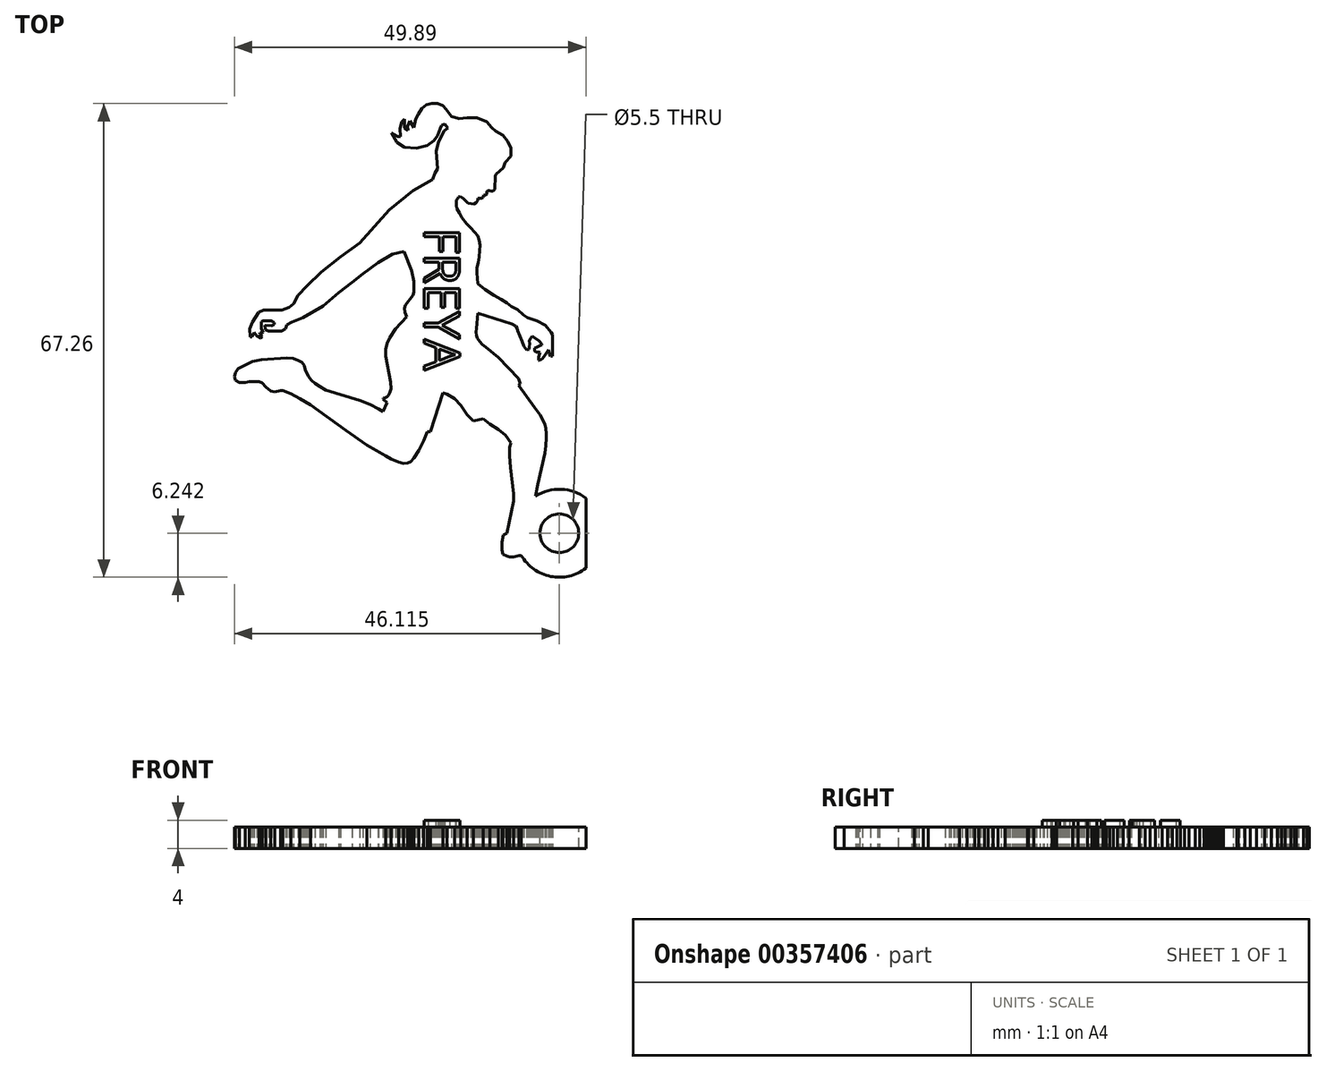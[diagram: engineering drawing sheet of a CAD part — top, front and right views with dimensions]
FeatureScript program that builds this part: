
annotation { "Feature Type Name" : "Feature", "Feature Type Description" : "" }
export const myFeature = defineFeature(function(context is Context, id is Id, definition is map)
    precondition{}
    {
        {
            var Q0;
            Q0=qCreatedBy(makeId("Top.planeOp"),FACE);
            var sketch = newSketch(context, id + "F0", { "sketchPlane" : qUnion([Q0])});
            skLineSegment(sketch, "E0.bottom", {"start": v(0, 0) * mm, "end": v(-50, 0) * mm});
            skLineSegment(sketch, "E0.top", {"start": v(0, 70) * mm, "end": v(-50, 70) * mm});
            skLineSegment(sketch, "E0.left", {"start": v(0, 0) * mm, "end": v(0, 70) * mm});
            skLineSegment(sketch, "E0.right", {"start": v(-50, 0) * mm, "end": v(-50, 70) * mm});
            skLineSegment(sketch, "E1", {"start": v(-9.17, 3.5) * mm, "end": v(-9.48, 3.47) * mm});
            skLineSegment(sketch, "E2", {"start": v(-9.48, 3.47) * mm, "end": v(-10.25, 3.32) * mm});
            skLineSegment(sketch, "E3", {"start": v(-10.25, 3.32) * mm, "end": v(-10.82, 3.32) * mm});
            skLineSegment(sketch, "E4", {"start": v(-10.82, 3.32) * mm, "end": v(-11.24, 3.4) * mm});
            skLineSegment(sketch, "E5", {"start": v(-11.24, 3.4) * mm, "end": v(-11.78, 3.7) * mm});
            skLineSegment(sketch, "E6", {"start": v(-11.78, 3.7) * mm, "end": v(-11.9, 4.28) * mm});
            skLineSegment(sketch, "E7", {"start": v(-11.9, 4.28) * mm, "end": v(-11.9, 5.38) * mm});
            skLineSegment(sketch, "E8", {"start": v(-11.9, 5.38) * mm, "end": v(-11.72, 6.39) * mm});
            skLineSegment(sketch, "E9", {"start": v(-11.72, 6.39) * mm, "end": v(-11.24, 6.64) * mm});
            skLineSegment(sketch, "E10", {"start": v(-11.24, 6.64) * mm, "end": v(-10.25, 11.21) * mm});
            skLineSegment(sketch, "E11", {"start": v(-10.25, 11.21) * mm, "end": v(-10.25, 12.25) * mm});
            skLineSegment(sketch, "E12", {"start": v(-10.25, 12.25) * mm, "end": v(-10.74, 16) * mm});
            skLineSegment(sketch, "E13", {"start": v(-10.74, 16) * mm, "end": v(-10.86, 17.66) * mm});
            skLineSegment(sketch, "E14", {"start": v(-10.86, 17.66) * mm, "end": v(-10.86, 18.84) * mm});
            skLineSegment(sketch, "E15", {"start": v(-10.86, 18.84) * mm, "end": v(-10.66, 19.47) * mm});
            skLineSegment(sketch, "E16", {"start": v(-10.66, 19.47) * mm, "end": v(-11.4, 20.54) * mm});
            skLineSegment(sketch, "E17", {"start": v(-11.4, 20.54) * mm, "end": v(-12.4, 21.37) * mm});
            skLineSegment(sketch, "E18", {"start": v(-12.4, 21.37) * mm, "end": v(-13.64, 22.17) * mm});
            skLineSegment(sketch, "E19", {"start": v(-13.64, 22.17) * mm, "end": v(-14.55, 22.92) * mm});
            skLineSegment(sketch, "E20", {"start": v(-14.55, 22.92) * mm, "end": v(-16, 22.57) * mm});
            skLineSegment(sketch, "E21", {"start": v(-16, 22.57) * mm, "end": v(-16.9, 23.46) * mm});
            skLineSegment(sketch, "E22", {"start": v(-16.9, 23.46) * mm, "end": v(-17.76, 24.82) * mm});
            skLineSegment(sketch, "E23", {"start": v(-17.76, 24.82) * mm, "end": v(-18.67, 25.75) * mm});
            skLineSegment(sketch, "E24", {"start": v(-18.67, 25.75) * mm, "end": v(-19.72, 26.43) * mm});
            skLineSegment(sketch, "E25", {"start": v(-19.72, 26.43) * mm, "end": v(-20.3, 26.61) * mm});
            skLineSegment(sketch, "E26", {"start": v(-20.3, 26.61) * mm, "end": v(-22.05, 21.07) * mm});
            skLineSegment(sketch, "E27", {"start": v(-22.05, 21.07) * mm, "end": v(-22.5, 21.07) * mm});
            skLineSegment(sketch, "E28", {"start": v(-22.5, 21.07) * mm, "end": v(-23.04, 19.78) * mm});
            skLineSegment(sketch, "E29", {"start": v(-23.04, 19.78) * mm, "end": v(-23.74, 18.43) * mm});
            skLineSegment(sketch, "E30", {"start": v(-23.74, 18.43) * mm, "end": v(-24.44, 17.35) * mm});
            skLineSegment(sketch, "E31", {"start": v(-24.44, 17.35) * mm, "end": v(-24.87, 16.83) * mm});
            skLineSegment(sketch, "E32", {"start": v(-24.87, 16.83) * mm, "end": v(-25.32, 16.62) * mm});
            skLineSegment(sketch, "E33", {"start": v(-25.32, 16.62) * mm, "end": v(-25.92, 16.57) * mm});
            skLineSegment(sketch, "E34", {"start": v(-25.92, 16.57) * mm, "end": v(-26.6, 16.74) * mm});
            skLineSegment(sketch, "E35", {"start": v(-26.6, 16.74) * mm, "end": v(-27.67, 17.2) * mm});
            skLineSegment(sketch, "E36", {"start": v(-27.67, 17.2) * mm, "end": v(-28.42, 17.62) * mm});
            skLineSegment(sketch, "E37", {"start": v(-28.42, 17.62) * mm, "end": v(-31.07, 19.17) * mm});
            skLineSegment(sketch, "E38", {"start": v(-31.07, 19.17) * mm, "end": v(-34.05, 21.3) * mm});
            skLineSegment(sketch, "E39", {"start": v(-34.05, 21.3) * mm, "end": v(-39.1, 24.9) * mm});
            skLineSegment(sketch, "E40", {"start": v(-39.1, 24.9) * mm, "end": v(-40.6, 25.77) * mm});
            skLineSegment(sketch, "E41", {"start": v(-40.6, 25.77) * mm, "end": v(-41.87, 26.48) * mm});
            skLineSegment(sketch, "E42", {"start": v(-41.87, 26.48) * mm, "end": v(-43.02, 26.92) * mm});
            skLineSegment(sketch, "E43", {"start": v(-43.02, 26.92) * mm, "end": v(-43.33, 26.92) * mm});
            skLineSegment(sketch, "E44", {"start": v(-43.33, 26.92) * mm, "end": v(-44.18, 26.75) * mm});
            skLineSegment(sketch, "E45", {"start": v(-44.18, 26.75) * mm, "end": v(-44.78, 26.85) * mm});
            skLineSegment(sketch, "E46", {"start": v(-44.78, 26.85) * mm, "end": v(-45.47, 27.43) * mm});
            skLineSegment(sketch, "E47", {"start": v(-45.47, 27.43) * mm, "end": v(-45.94, 27.98) * mm});
            skLineSegment(sketch, "E48", {"start": v(-45.94, 27.98) * mm, "end": v(-46.39, 28.18) * mm});
            skLineSegment(sketch, "E49", {"start": v(-46.39, 28.18) * mm, "end": v(-47.08, 28.18) * mm});
            skLineSegment(sketch, "E50", {"start": v(-47.08, 28.18) * mm, "end": v(-47.78, 28.18) * mm});
            skLineSegment(sketch, "E51", {"start": v(-47.78, 28.18) * mm, "end": v(-48.35, 28.04) * mm});
            skLineSegment(sketch, "E52", {"start": v(-48.35, 28.04) * mm, "end": v(-49.18, 28.04) * mm});
            skLineSegment(sketch, "E53", {"start": v(-49.18, 28.04) * mm, "end": v(-49.76, 28.37) * mm});
            skLineSegment(sketch, "E54", {"start": v(-49.76, 28.37) * mm, "end": v(-49.9, 28.9) * mm});
            skLineSegment(sketch, "E55", {"start": v(-49.9, 28.9) * mm, "end": v(-49.8, 29.43) * mm});
            skLineSegment(sketch, "E56", {"start": v(-49.8, 29.43) * mm, "end": v(-49.4, 30.04) * mm});
            skLineSegment(sketch, "E57", {"start": v(-49.4, 30.04) * mm, "end": v(-48.36, 30.54) * mm});
            skLineSegment(sketch, "E58", {"start": v(-48.36, 30.54) * mm, "end": v(-47.36, 31.02) * mm});
            skLineSegment(sketch, "E59", {"start": v(-47.36, 31.02) * mm, "end": v(-46.1, 31.27) * mm});
            skLineSegment(sketch, "E60", {"start": v(-46.1, 31.27) * mm, "end": v(-44.89, 31.37) * mm});
            skLineSegment(sketch, "E61", {"start": v(-44.89, 31.37) * mm, "end": v(-43.62, 31.47) * mm});
            skLineSegment(sketch, "E62", {"start": v(-43.62, 31.47) * mm, "end": v(-42.48, 31.56) * mm});
            skLineSegment(sketch, "E63", {"start": v(-42.48, 31.56) * mm, "end": v(-41.57, 31.5) * mm});
            skLineSegment(sketch, "E64", {"start": v(-41.57, 31.5) * mm, "end": v(-40.79, 31.19) * mm});
            skLineSegment(sketch, "E65", {"start": v(-40.79, 31.19) * mm, "end": v(-40.32, 30.92) * mm});
            skLineSegment(sketch, "E66", {"start": v(-40.32, 30.92) * mm, "end": v(-40, 30.5) * mm});
            skLineSegment(sketch, "E67", {"start": v(-40, 30.5) * mm, "end": v(-39.86, 29.9) * mm});
            skLineSegment(sketch, "E68", {"start": v(-39.86, 29.9) * mm, "end": v(-39.65, 29.47) * mm});
            skLineSegment(sketch, "E69", {"start": v(-39.65, 29.47) * mm, "end": v(-39.4, 28.93) * mm});
            skLineSegment(sketch, "E70", {"start": v(-39.4, 28.93) * mm, "end": v(-38.97, 28.35) * mm});
            skLineSegment(sketch, "E71", {"start": v(-38.97, 28.35) * mm, "end": v(-38.46, 27.9) * mm});
            skLineSegment(sketch, "E72", {"start": v(-38.46, 27.9) * mm, "end": v(-37.78, 27.46) * mm});
            skLineSegment(sketch, "E73", {"start": v(-37.78, 27.46) * mm, "end": v(-36.91, 27) * mm});
            skLineSegment(sketch, "E74", {"start": v(-36.91, 27) * mm, "end": v(-35.94, 26.7) * mm});
            skLineSegment(sketch, "E75", {"start": v(-35.94, 26.7) * mm, "end": v(-34.76, 26.33) * mm});
            skLineSegment(sketch, "E76", {"start": v(-34.76, 26.33) * mm, "end": v(-32.12, 25.5) * mm});
            skLineSegment(sketch, "E77", {"start": v(-32.12, 25.5) * mm, "end": v(-30.66, 24.93) * mm});
            skLineSegment(sketch, "E78", {"start": v(-30.66, 24.93) * mm, "end": v(-29.45, 24.33) * mm});
            skLineSegment(sketch, "E79", {"start": v(-29.45, 24.33) * mm, "end": v(-28.83, 23.93) * mm});
            skLineSegment(sketch, "E80", {"start": v(-28.83, 23.93) * mm, "end": v(-28.21, 25.2) * mm});
            skLineSegment(sketch, "E81", {"start": v(-28.21, 25.2) * mm, "end": v(-28.82, 25.7) * mm});
            skLineSegment(sketch, "E82", {"start": v(-28.82, 25.7) * mm, "end": v(-28.76, 25.81) * mm});
            skLineSegment(sketch, "E83", {"start": v(-28.76, 25.81) * mm, "end": v(-28.5, 25.88) * mm});
            skLineSegment(sketch, "E84", {"start": v(-28.5, 25.88) * mm, "end": v(-28.24, 26) * mm});
            skLineSegment(sketch, "E85", {"start": v(-28.24, 26) * mm, "end": v(-28.06, 26.23) * mm});
            skLineSegment(sketch, "E86", {"start": v(-28.06, 26.23) * mm, "end": v(-27.83, 26.57) * mm});
            skLineSegment(sketch, "E87", {"start": v(-27.83, 26.57) * mm, "end": v(-27.65, 27.16) * mm});
            skLineSegment(sketch, "E88", {"start": v(-27.65, 27.16) * mm, "end": v(-27.72, 28.1) * mm});
            skLineSegment(sketch, "E89", {"start": v(-27.72, 28.1) * mm, "end": v(-27.93, 29.16) * mm});
            skLineSegment(sketch, "E90", {"start": v(-27.93, 29.16) * mm, "end": v(-28.21, 30.56) * mm});
            skLineSegment(sketch, "E91", {"start": v(-28.21, 30.56) * mm, "end": v(-28.46, 31.8) * mm});
            skLineSegment(sketch, "E92", {"start": v(-28.46, 31.8) * mm, "end": v(-28.4, 32.79) * mm});
            skLineSegment(sketch, "E93", {"start": v(-28.4, 32.79) * mm, "end": v(-28.21, 33.59) * mm});
            skLineSegment(sketch, "E94", {"start": v(-28.21, 33.59) * mm, "end": v(-27.88, 34.42) * mm});
            skLineSegment(sketch, "E95", {"start": v(-27.88, 34.42) * mm, "end": v(-27.04, 35.7) * mm});
            skLineSegment(sketch, "E96", {"start": v(-27.04, 35.7) * mm, "end": v(-25.43, 37.42) * mm});
            skLineSegment(sketch, "E97", {"start": v(-25.43, 37.42) * mm, "end": v(-25.71, 38) * mm});
            skLineSegment(sketch, "E98", {"start": v(-25.71, 38) * mm, "end": v(-25.76, 38.6) * mm});
            skLineSegment(sketch, "E99", {"start": v(-25.76, 38.6) * mm, "end": v(-25.65, 39.06) * mm});
            skLineSegment(sketch, "E100", {"start": v(-25.65, 39.06) * mm, "end": v(-25.11, 39.71) * mm});
            skLineSegment(sketch, "E101", {"start": v(-25.11, 39.71) * mm, "end": v(-24.53, 40.43) * mm});
            skLineSegment(sketch, "E102", {"start": v(-24.53, 40.43) * mm, "end": v(-24.44, 40.9) * mm});
            skLineSegment(sketch, "E103", {"start": v(-24.44, 40.9) * mm, "end": v(-24.44, 42.39) * mm});
            skLineSegment(sketch, "E104", {"start": v(-24.44, 42.39) * mm, "end": v(-24.74, 43.9) * mm});
            skLineSegment(sketch, "E105", {"start": v(-24.74, 43.9) * mm, "end": v(-25.83, 46.69) * mm});
            skLineSegment(sketch, "E106", {"start": v(-25.83, 46.69) * mm, "end": v(-27.46, 46.29) * mm});
            skLineSegment(sketch, "E107", {"start": v(-27.46, 46.29) * mm, "end": v(-29.5, 45.05) * mm});
            skLineSegment(sketch, "E108", {"start": v(-29.5, 45.05) * mm, "end": v(-31.65, 43.48) * mm});
            skLineSegment(sketch, "E109", {"start": v(-31.65, 43.48) * mm, "end": v(-33.2, 42.3) * mm});
            skLineSegment(sketch, "E110", {"start": v(-33.2, 42.3) * mm, "end": v(-35.08, 40.8) * mm});
            skLineSegment(sketch, "E111", {"start": v(-35.08, 40.8) * mm, "end": v(-37.3, 38.93) * mm});
            skLineSegment(sketch, "E112", {"start": v(-37.3, 38.93) * mm, "end": v(-40.15, 37.27) * mm});
            skLineSegment(sketch, "E113", {"start": v(-40.15, 37.27) * mm, "end": v(-41.8, 36.64) * mm});
            skLineSegment(sketch, "E114", {"start": v(-41.8, 36.64) * mm, "end": v(-42.44, 36.27) * mm});
            skLineSegment(sketch, "E115", {"start": v(-42.44, 36.27) * mm, "end": v(-42.67, 35.69) * mm});
            skLineSegment(sketch, "E116", {"start": v(-42.67, 35.69) * mm, "end": v(-43.2, 35.37) * mm});
            skLineSegment(sketch, "E117", {"start": v(-43.2, 35.37) * mm, "end": v(-45.06, 35.37) * mm});
            skLineSegment(sketch, "E118", {"start": v(-45.06, 35.37) * mm, "end": v(-45.52, 35.56) * mm});
            skLineSegment(sketch, "E119", {"start": v(-45.52, 35.56) * mm, "end": v(-45.57, 36.16) * mm});
            skLineSegment(sketch, "E120", {"start": v(-45.57, 36.16) * mm, "end": v(-44.6, 36.1) * mm});
            skLineSegment(sketch, "E121", {"start": v(-44.6, 36.1) * mm, "end": v(-44.22, 36.28) * mm});
            skLineSegment(sketch, "E122", {"start": v(-44.22, 36.28) * mm, "end": v(-44.22, 36.58) * mm});
            skLineSegment(sketch, "E123", {"start": v(-44.22, 36.58) * mm, "end": v(-44.69, 36.85) * mm});
            skLineSegment(sketch, "E124", {"start": v(-44.69, 36.85) * mm, "end": v(-45.84, 36.8) * mm});
            skLineSegment(sketch, "E125", {"start": v(-45.84, 36.8) * mm, "end": v(-46.08, 36.67) * mm});
            skLineSegment(sketch, "E126", {"start": v(-46.08, 36.67) * mm, "end": v(-46.08, 35.72) * mm});
            skLineSegment(sketch, "E127", {"start": v(-46.08, 35.72) * mm, "end": v(-45.82, 35.2) * mm});
            skLineSegment(sketch, "E128", {"start": v(-45.82, 35.2) * mm, "end": v(-45.87, 35.08) * mm});
            skLineSegment(sketch, "E129", {"start": v(-45.87, 35.08) * mm, "end": v(-46.27, 35.08) * mm});
            skLineSegment(sketch, "E130", {"start": v(-46.27, 35.08) * mm, "end": v(-46.3, 34.93) * mm});
            skLineSegment(sketch, "E131", {"start": v(-46.3, 34.93) * mm, "end": v(-45.94, 34.61) * mm});
            skLineSegment(sketch, "E132", {"start": v(-45.94, 34.61) * mm, "end": v(-46.16, 34.34) * mm});
            skLineSegment(sketch, "E133", {"start": v(-46.16, 34.34) * mm, "end": v(-46.7, 34.65) * mm});
            skLineSegment(sketch, "E134", {"start": v(-46.7, 34.65) * mm, "end": v(-47.11, 35.15) * mm});
            skLineSegment(sketch, "E135", {"start": v(-47.11, 35.15) * mm, "end": v(-47.42, 34.54) * mm});
            skLineSegment(sketch, "E136", {"start": v(-47.42, 34.54) * mm, "end": v(-47.66, 34.54) * mm});
            skLineSegment(sketch, "E137", {"start": v(-47.66, 34.54) * mm, "end": v(-47.76, 35.69) * mm});
            skLineSegment(sketch, "E138", {"start": v(-47.76, 35.69) * mm, "end": v(-47.37, 36.65) * mm});
            skLineSegment(sketch, "E139", {"start": v(-47.37, 36.65) * mm, "end": v(-46.5, 38) * mm});
            skLineSegment(sketch, "E140", {"start": v(-46.5, 38) * mm, "end": v(-45.76, 38.35) * mm});
            skLineSegment(sketch, "E141", {"start": v(-45.76, 38.35) * mm, "end": v(-43.14, 38.35) * mm});
            skLineSegment(sketch, "E142", {"start": v(-43.14, 38.35) * mm, "end": v(-42.18, 38.72) * mm});
            skLineSegment(sketch, "E143", {"start": v(-42.18, 38.72) * mm, "end": v(-41.51, 39.25) * mm});
            skLineSegment(sketch, "E144", {"start": v(-41.51, 39.25) * mm, "end": v(-40.85, 40.43) * mm});
            skLineSegment(sketch, "E145", {"start": v(-40.85, 40.43) * mm, "end": v(-39.6, 41.78) * mm});
            skLineSegment(sketch, "E146", {"start": v(-39.6, 41.78) * mm, "end": v(-37.56, 43.72) * mm});
            skLineSegment(sketch, "E147", {"start": v(-37.56, 43.72) * mm, "end": v(-34.86, 45.88) * mm});
            skLineSegment(sketch, "E148", {"start": v(-34.86, 45.88) * mm, "end": v(-32.12, 47.88) * mm});
            skLineSegment(sketch, "E149", {"start": v(-32.12, 47.88) * mm, "end": v(-27.93, 52.55) * mm});
            skLineSegment(sketch, "E150", {"start": v(-27.93, 52.55) * mm, "end": v(-24.53, 55.27) * mm});
            skLineSegment(sketch, "E151", {"start": v(-24.53, 55.27) * mm, "end": v(-21.79, 56.87) * mm});
            skLineSegment(sketch, "E152", {"start": v(-21.79, 56.87) * mm, "end": v(-21.43, 57.77) * mm});
            skLineSegment(sketch, "E153", {"start": v(-21.43, 57.77) * mm, "end": v(-21.03, 58.38) * mm});
            skLineSegment(sketch, "E154", {"start": v(-21.03, 58.38) * mm, "end": v(-21.23, 60.88) * mm});
            skLineSegment(sketch, "E155", {"start": v(-21.23, 60.88) * mm, "end": v(-20.92, 62.2) * mm});
            skLineSegment(sketch, "E156", {"start": v(-20.92, 62.2) * mm, "end": v(-20.5, 63.07) * mm});
            skLineSegment(sketch, "E157", {"start": v(-20.5, 63.07) * mm, "end": v(-20.13, 63.82) * mm});
            skLineSegment(sketch, "E158", {"start": v(-20.13, 63.82) * mm, "end": v(-19.63, 64.22) * mm});
            skLineSegment(sketch, "E159", {"start": v(-19.63, 64.22) * mm, "end": v(-20.06, 64.75) * mm});
            skLineSegment(sketch, "E160", {"start": v(-20.06, 64.75) * mm, "end": v(-20.5, 64.54) * mm});
            skLineSegment(sketch, "E161", {"start": v(-20.5, 64.54) * mm, "end": v(-20.7, 64.13) * mm});
            skLineSegment(sketch, "E162", {"start": v(-20.7, 64.13) * mm, "end": v(-21.03, 63.08) * mm});
            skLineSegment(sketch, "E163", {"start": v(-21.03, 63.08) * mm, "end": v(-21.56, 62.44) * mm});
            skLineSegment(sketch, "E164", {"start": v(-21.56, 62.44) * mm, "end": v(-22.5, 61.68) * mm});
            skLineSegment(sketch, "E165", {"start": v(-22.5, 61.68) * mm, "end": v(-24.04, 61.3) * mm});
            skLineSegment(sketch, "E166", {"start": v(-24.04, 61.3) * mm, "end": v(-25.76, 61.46) * mm});
            skLineSegment(sketch, "E167", {"start": v(-25.76, 61.46) * mm, "end": v(-26.81, 62.15) * mm});
            skLineSegment(sketch, "E168", {"start": v(-26.81, 62.15) * mm, "end": v(-27.6, 63.51) * mm});
            skLineSegment(sketch, "E169", {"start": v(-27.6, 63.51) * mm, "end": v(-26.72, 63) * mm});
            skLineSegment(sketch, "E170", {"start": v(-26.72, 63) * mm, "end": v(-26.35, 63) * mm});
            skLineSegment(sketch, "E171", {"start": v(-26.35, 63) * mm, "end": v(-26.4, 64.13) * mm});
            skLineSegment(sketch, "E172", {"start": v(-26.4, 64.13) * mm, "end": v(-26.14, 65.05) * mm});
            skLineSegment(sketch, "E173", {"start": v(-26.14, 65.05) * mm, "end": v(-25.76, 65.44) * mm});
            skLineSegment(sketch, "E174", {"start": v(-25.76, 65.44) * mm, "end": v(-25.76, 64.64) * mm});
            skLineSegment(sketch, "E175", {"start": v(-25.76, 64.64) * mm, "end": v(-25.76, 64.19) * mm});
            skLineSegment(sketch, "E176", {"start": v(-25.76, 64.19) * mm, "end": v(-25.29, 63.88) * mm});
            skLineSegment(sketch, "E177", {"start": v(-25.29, 63.88) * mm, "end": v(-25.33, 64.43) * mm});
            skLineSegment(sketch, "E178", {"start": v(-25.33, 64.43) * mm, "end": v(-25, 65.17) * mm});
            skLineSegment(sketch, "E179", {"start": v(-25, 65.17) * mm, "end": v(-24.44, 64.22) * mm});
            skLineSegment(sketch, "E180", {"start": v(-24.44, 64.22) * mm, "end": v(-24.16, 65.43) * mm});
            skLineSegment(sketch, "E181", {"start": v(-24.16, 65.43) * mm, "end": v(-23.8, 66.17) * mm});
            skLineSegment(sketch, "E182", {"start": v(-23.8, 66.17) * mm, "end": v(-23.26, 67) * mm});
            skLineSegment(sketch, "E183", {"start": v(-23.26, 67) * mm, "end": v(-22.65, 67.48) * mm});
            skLineSegment(sketch, "E184", {"start": v(-22.65, 67.48) * mm, "end": v(-21.89, 67.67) * mm});
            skLineSegment(sketch, "E185", {"start": v(-21.89, 67.67) * mm, "end": v(-21.04, 67.66) * mm});
            skLineSegment(sketch, "E186", {"start": v(-21.04, 67.66) * mm, "end": v(-20.3, 67.4) * mm});
            skLineSegment(sketch, "E187", {"start": v(-20.3, 67.4) * mm, "end": v(-19.86, 66.83) * mm});
            skLineSegment(sketch, "E188", {"start": v(-19.86, 66.83) * mm, "end": v(-19.09, 65.86) * mm});
            skLineSegment(sketch, "E189", {"start": v(-19.09, 65.86) * mm, "end": v(-18.02, 65.52) * mm});
            skLineSegment(sketch, "E190", {"start": v(-18.02, 65.52) * mm, "end": v(-16.84, 65.62) * mm});
            skLineSegment(sketch, "E191", {"start": v(-16.84, 65.62) * mm, "end": v(-15.47, 65.62) * mm});
            skLineSegment(sketch, "E192", {"start": v(-15.47, 65.62) * mm, "end": v(-14.09, 65.06) * mm});
            skLineSegment(sketch, "E193", {"start": v(-14.09, 65.06) * mm, "end": v(-13.36, 64.27) * mm});
            skLineSegment(sketch, "E194", {"start": v(-13.36, 64.27) * mm, "end": v(-12.84, 63.75) * mm});
            skLineSegment(sketch, "E195", {"start": v(-12.84, 63.75) * mm, "end": v(-11.78, 63.15) * mm});
            skLineSegment(sketch, "E196", {"start": v(-11.78, 63.15) * mm, "end": v(-11.1, 62.3) * mm});
            skLineSegment(sketch, "E197", {"start": v(-11.1, 62.3) * mm, "end": v(-10.62, 61.3) * mm});
            skLineSegment(sketch, "E198", {"start": v(-10.62, 61.3) * mm, "end": v(-10.62, 60.2) * mm});
            skLineSegment(sketch, "E199", {"start": v(-10.62, 60.2) * mm, "end": v(-11.5, 59.28) * mm});
            skLineSegment(sketch, "E200", {"start": v(-11.5, 59.28) * mm, "end": v(-11.73, 58.55) * mm});
            skLineSegment(sketch, "E201", {"start": v(-11.73, 58.55) * mm, "end": v(-12.75, 57.62) * mm});
            skLineSegment(sketch, "E202", {"start": v(-12.75, 57.62) * mm, "end": v(-12.87, 57.37) * mm});
            skLineSegment(sketch, "E203", {"start": v(-12.87, 57.37) * mm, "end": v(-12.95, 55.5) * mm});
            skLineSegment(sketch, "E204", {"start": v(-12.95, 55.5) * mm, "end": v(-13.03, 55.35) * mm});
            skLineSegment(sketch, "E205", {"start": v(-13.03, 55.35) * mm, "end": v(-13.19, 55.22) * mm});
            skLineSegment(sketch, "E206", {"start": v(-13.19, 55.22) * mm, "end": v(-13.42, 55.22) * mm});
            skLineSegment(sketch, "E207", {"start": v(-13.42, 55.22) * mm, "end": v(-13.68, 55.27) * mm});
            skLineSegment(sketch, "E208", {"start": v(-13.68, 55.27) * mm, "end": v(-13.95, 55.27) * mm});
            skLineSegment(sketch, "E209", {"start": v(-13.95, 55.27) * mm, "end": v(-14.04, 55.22) * mm});
            skLineSegment(sketch, "E210", {"start": v(-14.04, 55.22) * mm, "end": v(-14.08, 55.02) * mm});
            skLineSegment(sketch, "E211", {"start": v(-14.08, 55.02) * mm, "end": v(-14.08, 54.8) * mm});
            skLineSegment(sketch, "E212", {"start": v(-14.08, 54.8) * mm, "end": v(-14.2, 54.7) * mm});
            skLineSegment(sketch, "E213", {"start": v(-14.2, 54.7) * mm, "end": v(-14.53, 54.67) * mm});
            skLineSegment(sketch, "E214", {"start": v(-14.53, 54.67) * mm, "end": v(-14.59, 54.36) * mm});
            skLineSegment(sketch, "E215", {"start": v(-14.59, 54.36) * mm, "end": v(-14.7, 54.25) * mm});
            skLineSegment(sketch, "E216", {"start": v(-14.7, 54.25) * mm, "end": v(-14.85, 54.2) * mm});
            skLineSegment(sketch, "E217", {"start": v(-14.85, 54.2) * mm, "end": v(-15.37, 54.2) * mm});
            skLineSegment(sketch, "E218", {"start": v(-15.37, 54.2) * mm, "end": v(-15.34, 53.88) * mm});
            skLineSegment(sketch, "E219", {"start": v(-15.34, 53.88) * mm, "end": v(-15.58, 53.57) * mm});
            skLineSegment(sketch, "E220", {"start": v(-15.58, 53.57) * mm, "end": v(-15.92, 53.4) * mm});
            skLineSegment(sketch, "E221", {"start": v(-15.92, 53.4) * mm, "end": v(-16.32, 53.45) * mm});
            skLineSegment(sketch, "E222", {"start": v(-16.32, 53.45) * mm, "end": v(-16.73, 53.53) * mm});
            skLineSegment(sketch, "E223", {"start": v(-16.73, 53.53) * mm, "end": v(-17.08, 53.82) * mm});
            skLineSegment(sketch, "E224", {"start": v(-17.08, 53.82) * mm, "end": v(-17.4, 54.12) * mm});
            skLineSegment(sketch, "E225", {"start": v(-17.4, 54.12) * mm, "end": v(-17.62, 54.37) * mm});
            skLineSegment(sketch, "E226", {"start": v(-17.62, 54.37) * mm, "end": v(-17.83, 54.47) * mm});
            skLineSegment(sketch, "E227", {"start": v(-17.83, 54.47) * mm, "end": v(-18.06, 54.41) * mm});
            skLineSegment(sketch, "E228", {"start": v(-18.06, 54.41) * mm, "end": v(-18.21, 54.15) * mm});
            skLineSegment(sketch, "E229", {"start": v(-18.21, 54.15) * mm, "end": v(-18.38, 53.94) * mm});
            skLineSegment(sketch, "E230", {"start": v(-18.38, 53.94) * mm, "end": v(-18.43, 53.67) * mm});
            skLineSegment(sketch, "E231", {"start": v(-18.43, 53.67) * mm, "end": v(-18.39, 53.2) * mm});
            skLineSegment(sketch, "E232", {"start": v(-18.39, 53.2) * mm, "end": v(-18.3, 52.76) * mm});
            skLineSegment(sketch, "E233", {"start": v(-18.3, 52.76) * mm, "end": v(-17.93, 52.1) * mm});
            skLineSegment(sketch, "E234", {"start": v(-17.93, 52.1) * mm, "end": v(-17.62, 51.46) * mm});
            skLineSegment(sketch, "E235", {"start": v(-17.62, 51.46) * mm, "end": v(-16.95, 50.63) * mm});
            skLineSegment(sketch, "E236", {"start": v(-16.95, 50.63) * mm, "end": v(-16.35, 50) * mm});
            skLineSegment(sketch, "E237", {"start": v(-16.35, 50) * mm, "end": v(-15.77, 49.42) * mm});
            skLineSegment(sketch, "E238", {"start": v(-15.77, 49.42) * mm, "end": v(-15.38, 48.9) * mm});
            skLineSegment(sketch, "E239", {"start": v(-15.38, 48.9) * mm, "end": v(-15.14, 48.22) * mm});
            skLineSegment(sketch, "E240", {"start": v(-15.14, 48.22) * mm, "end": v(-15.04, 47.53) * mm});
            skLineSegment(sketch, "E241", {"start": v(-15.04, 47.53) * mm, "end": v(-15.07, 46.8) * mm});
            skLineSegment(sketch, "E242", {"start": v(-15.07, 46.8) * mm, "end": v(-15.13, 45.87) * mm});
            skLineSegment(sketch, "E243", {"start": v(-15.13, 45.87) * mm, "end": v(-15.27, 45.06) * mm});
            skLineSegment(sketch, "E244", {"start": v(-15.27, 45.06) * mm, "end": v(-15.48, 44.4) * mm});
            skLineSegment(sketch, "E245", {"start": v(-15.48, 44.4) * mm, "end": v(-15.45, 43.59) * mm});
            skLineSegment(sketch, "E246", {"start": v(-15.45, 43.59) * mm, "end": v(-15.38, 42.71) * mm});
            skLineSegment(sketch, "E247", {"start": v(-15.38, 42.71) * mm, "end": v(-15.34, 42.1) * mm});
            skLineSegment(sketch, "E248", {"start": v(-15.34, 42.1) * mm, "end": v(-14.31, 41.26) * mm});
            skLineSegment(sketch, "E249", {"start": v(-14.31, 41.26) * mm, "end": v(-13.09, 40.43) * mm});
            skLineSegment(sketch, "E250", {"start": v(-13.09, 40.43) * mm, "end": v(-12.07, 39.87) * mm});
            skLineSegment(sketch, "E251", {"start": v(-12.07, 39.87) * mm, "end": v(-11.24, 39.35) * mm});
            skLineSegment(sketch, "E252", {"start": v(-11.24, 39.35) * mm, "end": v(-10.57, 38.84) * mm});
            skLineSegment(sketch, "E253", {"start": v(-10.57, 38.84) * mm, "end": v(-9.71, 38.39) * mm});
            skLineSegment(sketch, "E254", {"start": v(-9.71, 38.39) * mm, "end": v(-8.87, 37.67) * mm});
            skLineSegment(sketch, "E255", {"start": v(-8.87, 37.67) * mm, "end": v(-8.32, 37.28) * mm});
            skLineSegment(sketch, "E256", {"start": v(-8.32, 37.28) * mm, "end": v(-6.94, 36.85) * mm});
            skLineSegment(sketch, "E257", {"start": v(-6.94, 36.85) * mm, "end": v(-5.79, 36.17) * mm});
            skLineSegment(sketch, "E258", {"start": v(-5.79, 36.17) * mm, "end": v(-4.96, 35.15) * mm});
            skLineSegment(sketch, "E259", {"start": v(-4.96, 35.15) * mm, "end": v(-4.72, 34.85) * mm});
            skLineSegment(sketch, "E260", {"start": v(-4.72, 34.85) * mm, "end": v(-4.75, 34.08) * mm});
            skLineSegment(sketch, "E261", {"start": v(-4.75, 34.08) * mm, "end": v(-4.75, 33.59) * mm});
            skLineSegment(sketch, "E262", {"start": v(-4.75, 33.59) * mm, "end": v(-4.75, 31.8) * mm});
            skLineSegment(sketch, "E263", {"start": v(-4.75, 31.8) * mm, "end": v(-4.98, 31.8) * mm});
            skLineSegment(sketch, "E264", {"start": v(-4.98, 31.8) * mm, "end": v(-5.22, 32.11) * mm});
            skLineSegment(sketch, "E265", {"start": v(-5.22, 32.11) * mm, "end": v(-5.33, 32.68) * mm});
            skLineSegment(sketch, "E266", {"start": v(-5.33, 32.68) * mm, "end": v(-5.8, 31.94) * mm});
            skLineSegment(sketch, "E267", {"start": v(-5.8, 31.94) * mm, "end": v(-6.17, 31.48) * mm});
            skLineSegment(sketch, "E268", {"start": v(-6.17, 31.48) * mm, "end": v(-6.57, 31.16) * mm});
            skLineSegment(sketch, "E269", {"start": v(-6.57, 31.16) * mm, "end": v(-6.7, 31.2) * mm});
            skLineSegment(sketch, "E270", {"start": v(-6.7, 31.2) * mm, "end": v(-6.7, 31.68) * mm});
            skLineSegment(sketch, "E271", {"start": v(-6.7, 31.68) * mm, "end": v(-6.6, 32.1) * mm});
            skLineSegment(sketch, "E272", {"start": v(-6.6, 32.1) * mm, "end": v(-6.51, 32.28) * mm});
            skLineSegment(sketch, "E273", {"start": v(-6.51, 32.28) * mm, "end": v(-6.62, 32.38) * mm});
            skLineSegment(sketch, "E274", {"start": v(-6.62, 32.38) * mm, "end": v(-7.06, 32.38) * mm});
            skLineSegment(sketch, "E275", {"start": v(-7.06, 32.38) * mm, "end": v(-7.27, 32.47) * mm});
            skLineSegment(sketch, "E276", {"start": v(-7.27, 32.47) * mm, "end": v(-7.3, 32.68) * mm});
            skLineSegment(sketch, "E277", {"start": v(-7.3, 32.68) * mm, "end": v(-7.3, 32.95) * mm});
            skLineSegment(sketch, "E278", {"start": v(-7.3, 32.95) * mm, "end": v(-6.99, 33.1) * mm});
            skLineSegment(sketch, "E279", {"start": v(-6.99, 33.1) * mm, "end": v(-6.61, 33.28) * mm});
            skLineSegment(sketch, "E280", {"start": v(-6.61, 33.28) * mm, "end": v(-6.27, 33.36) * mm});
            skLineSegment(sketch, "E281", {"start": v(-6.27, 33.36) * mm, "end": v(-6.25, 33.53) * mm});
            skLineSegment(sketch, "E282", {"start": v(-6.25, 33.53) * mm, "end": v(-6.66, 33.96) * mm});
            skLineSegment(sketch, "E283", {"start": v(-6.66, 33.96) * mm, "end": v(-7.46, 34.54) * mm});
            skLineSegment(sketch, "E284", {"start": v(-7.46, 34.54) * mm, "end": v(-7.69, 34.61) * mm});
            skLineSegment(sketch, "E285", {"start": v(-7.69, 34.61) * mm, "end": v(-7.84, 34.34) * mm});
            skLineSegment(sketch, "E286", {"start": v(-7.84, 34.34) * mm, "end": v(-8.05, 33.99) * mm});
            skLineSegment(sketch, "E287", {"start": v(-8.05, 33.99) * mm, "end": v(-8, 33.59) * mm});
            skLineSegment(sketch, "E288", {"start": v(-8, 33.59) * mm, "end": v(-8.07, 33.04) * mm});
            skLineSegment(sketch, "E289", {"start": v(-8.07, 33.04) * mm, "end": v(-8.13, 32.74) * mm});
            skLineSegment(sketch, "E290", {"start": v(-8.13, 32.74) * mm, "end": v(-8.4, 32.7) * mm});
            skLineSegment(sketch, "E291", {"start": v(-8.4, 32.7) * mm, "end": v(-8.79, 33.17) * mm});
            skLineSegment(sketch, "E292", {"start": v(-8.79, 33.17) * mm, "end": v(-9.05, 33.92) * mm});
            skLineSegment(sketch, "E293", {"start": v(-9.05, 33.92) * mm, "end": v(-9.72, 35.45) * mm});
            skLineSegment(sketch, "E294", {"start": v(-9.72, 35.45) * mm, "end": v(-9.79, 35.75) * mm});
            skLineSegment(sketch, "E295", {"start": v(-9.79, 35.75) * mm, "end": v(-9.97, 36.06) * mm});
            skLineSegment(sketch, "E296", {"start": v(-9.97, 36.06) * mm, "end": v(-10.5, 36.37) * mm});
            skLineSegment(sketch, "E297", {"start": v(-10.5, 36.37) * mm, "end": v(-15.35, 37.9) * mm});
            skLineSegment(sketch, "E298", {"start": v(-15.35, 37.9) * mm, "end": v(-15.55, 35.75) * mm});
            skLineSegment(sketch, "E299", {"start": v(-15.55, 35.75) * mm, "end": v(-15.57, 35.21) * mm});
            skLineSegment(sketch, "E300", {"start": v(-15.57, 35.21) * mm, "end": v(-15.54, 34.74) * mm});
            skLineSegment(sketch, "E301", {"start": v(-15.54, 34.74) * mm, "end": v(-15.39, 34.34) * mm});
            skLineSegment(sketch, "E302", {"start": v(-15.39, 34.34) * mm, "end": v(-15.11, 33.9) * mm});
            skLineSegment(sketch, "E303", {"start": v(-15.11, 33.9) * mm, "end": v(-14.7, 33.47) * mm});
            skLineSegment(sketch, "E304", {"start": v(-14.7, 33.47) * mm, "end": v(-14.21, 33.1) * mm});
            skLineSegment(sketch, "E305", {"start": v(-14.21, 33.1) * mm, "end": v(-12.4, 31.6) * mm});
            skLineSegment(sketch, "E306", {"start": v(-12.4, 31.6) * mm, "end": v(-9.58, 28.6) * mm});
            skLineSegment(sketch, "E307", {"start": v(-9.58, 28.6) * mm, "end": v(-9.31, 27.84) * mm});
            skLineSegment(sketch, "E308", {"start": v(-9.31, 27.84) * mm, "end": v(-9.6, 27.66) * mm});
            skLineSegment(sketch, "E309", {"start": v(-9.6, 27.66) * mm, "end": v(-7.32, 24.5) * mm});
            skLineSegment(sketch, "E310", {"start": v(-7.32, 24.5) * mm, "end": v(-6.52, 23.46) * mm});
            skLineSegment(sketch, "E311", {"start": v(-6.52, 23.46) * mm, "end": v(-6.15, 22.79) * mm});
            skLineSegment(sketch, "E312", {"start": v(-6.15, 22.79) * mm, "end": v(-5.83, 22.1) * mm});
            skLineSegment(sketch, "E313", {"start": v(-5.83, 22.1) * mm, "end": v(-5.7, 21.57) * mm});
            skLineSegment(sketch, "E314", {"start": v(-5.7, 21.57) * mm, "end": v(-5.65, 20.78) * mm});
            skLineSegment(sketch, "E315", {"start": v(-5.65, 20.78) * mm, "end": v(-5.65, 20.19) * mm});
            skLineSegment(sketch, "E316", {"start": v(-5.65, 20.19) * mm, "end": v(-5.7, 19.1) * mm});
            skLineSegment(sketch, "E317", {"start": v(-5.7, 19.1) * mm, "end": v(-5.82, 18.05) * mm});
            skLineSegment(sketch, "E318", {"start": v(-5.82, 18.05) * mm, "end": v(-6.1, 16.82) * mm});
            skLineSegment(sketch, "E319", {"start": v(-6.1, 16.82) * mm, "end": v(-6.82, 13.57) * mm});
            skLineSegment(sketch, "E320", {"start": v(-6.82, 13.57) * mm, "end": v(-7.14, 11.91) * mm});
            skArc(sketch, "E321", {"start": v(-9.17, 3.5) * mm, "mid": v(2.3, 5.19) * mm, "end": v(-7.14, 11.91) * mm});
            skSolve(sketch);
        }
        {
            var Q0;
            {var subQ4=sQuery(id+"F0.wireOp",EDGE,"E1");Q0=makeQuery(id+"F0.imprint","IMPRINT",FACE,{"disambiguationData":[TD([[makeQuery(id+"F0.imprint","IMPRINT",EDGE,{"derivedFrom":subQ4}),-1.0]])]});}
            var Q1;
            {var subQ0=sQuery(id+"F0.wireOp",EDGE,"E321");var subQ1=sQuery(id+"F0.wireOp",EDGE,"E0.left");var subQ2=makeQuery(id+"F0.imprint","INTERSECT",VERTEX,{"disambiguationData":[OD(0.0)],"derivedFrom":[subQ1,subQ0]});Q1=makeQuery(id+"F0.imprint","IMPRINT",FACE,{"disambiguationData":[TD([[makeQuery(id+"F0.imprint","IMPRINT",EDGE,{"disambiguationData":[TD([[subQ2,-1.0]])],"derivedFrom":subQ1}),-1.0]])]});}
            extrude(context, id + "F1", {"entities" : qUnion([Q0, Q1]), "depth" : 3 * mm});
        }
        {
            var Q0;
            Q0=makeQuery(id+"F1.opExtrude","CAP_FACE",FACE,{"disambiguationData":[OSD([sQuery(id+"F0.wireOp",EDGE,"E1"),sQuery(id+"F0.wireOp",EDGE,"E2"),sQuery(id+"F0.wireOp",EDGE,"E3"),sQuery(id+"F0.wireOp",EDGE,"E4"),sQuery(id+"F0.wireOp",EDGE,"E5"),sQuery(id+"F0.wireOp",EDGE,"E6"),sQuery(id+"F0.wireOp",EDGE,"E7"),sQuery(id+"F0.wireOp",EDGE,"E8"),sQuery(id+"F0.wireOp",EDGE,"E9"),sQuery(id+"F0.wireOp",EDGE,"E10"),sQuery(id+"F0.wireOp",EDGE,"E11"),sQuery(id+"F0.wireOp",EDGE,"E12"),sQuery(id+"F0.wireOp",EDGE,"E13"),sQuery(id+"F0.wireOp",EDGE,"E14"),sQuery(id+"F0.wireOp",EDGE,"E15"),sQuery(id+"F0.wireOp",EDGE,"E16"),sQuery(id+"F0.wireOp",EDGE,"E17"),sQuery(id+"F0.wireOp",EDGE,"E18"),sQuery(id+"F0.wireOp",EDGE,"E19"),sQuery(id+"F0.wireOp",EDGE,"E20"),sQuery(id+"F0.wireOp",EDGE,"E21"),sQuery(id+"F0.wireOp",EDGE,"E22"),sQuery(id+"F0.wireOp",EDGE,"E23"),sQuery(id+"F0.wireOp",EDGE,"E24"),sQuery(id+"F0.wireOp",EDGE,"E25"),sQuery(id+"F0.wireOp",EDGE,"E26"),sQuery(id+"F0.wireOp",EDGE,"E27"),sQuery(id+"F0.wireOp",EDGE,"E28"),sQuery(id+"F0.wireOp",EDGE,"E29"),sQuery(id+"F0.wireOp",EDGE,"E30"),sQuery(id+"F0.wireOp",EDGE,"E31"),sQuery(id+"F0.wireOp",EDGE,"E32"),sQuery(id+"F0.wireOp",EDGE,"E33"),sQuery(id+"F0.wireOp",EDGE,"E34"),sQuery(id+"F0.wireOp",EDGE,"E35"),sQuery(id+"F0.wireOp",EDGE,"E36"),sQuery(id+"F0.wireOp",EDGE,"E37"),sQuery(id+"F0.wireOp",EDGE,"E38"),sQuery(id+"F0.wireOp",EDGE,"E39"),sQuery(id+"F0.wireOp",EDGE,"E40"),sQuery(id+"F0.wireOp",EDGE,"E41"),sQuery(id+"F0.wireOp",EDGE,"E42"),sQuery(id+"F0.wireOp",EDGE,"E43"),sQuery(id+"F0.wireOp",EDGE,"E44"),sQuery(id+"F0.wireOp",EDGE,"E45"),sQuery(id+"F0.wireOp",EDGE,"E46"),sQuery(id+"F0.wireOp",EDGE,"E47"),sQuery(id+"F0.wireOp",EDGE,"E48"),sQuery(id+"F0.wireOp",EDGE,"E49"),sQuery(id+"F0.wireOp",EDGE,"E50"),sQuery(id+"F0.wireOp",EDGE,"E51"),sQuery(id+"F0.wireOp",EDGE,"E52"),sQuery(id+"F0.wireOp",EDGE,"E53"),sQuery(id+"F0.wireOp",EDGE,"E54"),sQuery(id+"F0.wireOp",EDGE,"E55"),sQuery(id+"F0.wireOp",EDGE,"E56"),sQuery(id+"F0.wireOp",EDGE,"E57"),sQuery(id+"F0.wireOp",EDGE,"E58"),sQuery(id+"F0.wireOp",EDGE,"E59"),sQuery(id+"F0.wireOp",EDGE,"E60"),sQuery(id+"F0.wireOp",EDGE,"E61"),sQuery(id+"F0.wireOp",EDGE,"E62"),sQuery(id+"F0.wireOp",EDGE,"E63"),sQuery(id+"F0.wireOp",EDGE,"E64"),sQuery(id+"F0.wireOp",EDGE,"E65"),sQuery(id+"F0.wireOp",EDGE,"E66"),sQuery(id+"F0.wireOp",EDGE,"E67"),sQuery(id+"F0.wireOp",EDGE,"E68"),sQuery(id+"F0.wireOp",EDGE,"E69"),sQuery(id+"F0.wireOp",EDGE,"E70"),sQuery(id+"F0.wireOp",EDGE,"E71"),sQuery(id+"F0.wireOp",EDGE,"E72"),sQuery(id+"F0.wireOp",EDGE,"E73"),sQuery(id+"F0.wireOp",EDGE,"E74"),sQuery(id+"F0.wireOp",EDGE,"E75"),sQuery(id+"F0.wireOp",EDGE,"E76"),sQuery(id+"F0.wireOp",EDGE,"E77"),sQuery(id+"F0.wireOp",EDGE,"E78"),sQuery(id+"F0.wireOp",EDGE,"E79"),sQuery(id+"F0.wireOp",EDGE,"E80"),sQuery(id+"F0.wireOp",EDGE,"E81"),sQuery(id+"F0.wireOp",EDGE,"E82"),sQuery(id+"F0.wireOp",EDGE,"E83"),sQuery(id+"F0.wireOp",EDGE,"E84"),sQuery(id+"F0.wireOp",EDGE,"E85"),sQuery(id+"F0.wireOp",EDGE,"E86"),sQuery(id+"F0.wireOp",EDGE,"E87"),sQuery(id+"F0.wireOp",EDGE,"E88"),sQuery(id+"F0.wireOp",EDGE,"E89"),sQuery(id+"F0.wireOp",EDGE,"E90"),sQuery(id+"F0.wireOp",EDGE,"E91"),sQuery(id+"F0.wireOp",EDGE,"E92"),sQuery(id+"F0.wireOp",EDGE,"E93"),sQuery(id+"F0.wireOp",EDGE,"E94"),sQuery(id+"F0.wireOp",EDGE,"E95"),sQuery(id+"F0.wireOp",EDGE,"E96"),sQuery(id+"F0.wireOp",EDGE,"E97"),sQuery(id+"F0.wireOp",EDGE,"E98"),sQuery(id+"F0.wireOp",EDGE,"E99"),sQuery(id+"F0.wireOp",EDGE,"E100"),sQuery(id+"F0.wireOp",EDGE,"E101"),sQuery(id+"F0.wireOp",EDGE,"E102"),sQuery(id+"F0.wireOp",EDGE,"E103"),sQuery(id+"F0.wireOp",EDGE,"E104"),sQuery(id+"F0.wireOp",EDGE,"E105"),sQuery(id+"F0.wireOp",EDGE,"E106"),sQuery(id+"F0.wireOp",EDGE,"E107"),sQuery(id+"F0.wireOp",EDGE,"E108"),sQuery(id+"F0.wireOp",EDGE,"E109"),sQuery(id+"F0.wireOp",EDGE,"E110"),sQuery(id+"F0.wireOp",EDGE,"E111"),sQuery(id+"F0.wireOp",EDGE,"E112"),sQuery(id+"F0.wireOp",EDGE,"E113"),sQuery(id+"F0.wireOp",EDGE,"E114"),sQuery(id+"F0.wireOp",EDGE,"E115"),sQuery(id+"F0.wireOp",EDGE,"E116"),sQuery(id+"F0.wireOp",EDGE,"E117"),sQuery(id+"F0.wireOp",EDGE,"E118"),sQuery(id+"F0.wireOp",EDGE,"E119"),sQuery(id+"F0.wireOp",EDGE,"E120"),sQuery(id+"F0.wireOp",EDGE,"E121"),sQuery(id+"F0.wireOp",EDGE,"E122"),sQuery(id+"F0.wireOp",EDGE,"E123"),sQuery(id+"F0.wireOp",EDGE,"E124"),sQuery(id+"F0.wireOp",EDGE,"E125"),sQuery(id+"F0.wireOp",EDGE,"E126"),sQuery(id+"F0.wireOp",EDGE,"E127"),sQuery(id+"F0.wireOp",EDGE,"E128"),sQuery(id+"F0.wireOp",EDGE,"E129"),sQuery(id+"F0.wireOp",EDGE,"E130"),sQuery(id+"F0.wireOp",EDGE,"E131"),sQuery(id+"F0.wireOp",EDGE,"E132"),sQuery(id+"F0.wireOp",EDGE,"E133"),sQuery(id+"F0.wireOp",EDGE,"E134"),sQuery(id+"F0.wireOp",EDGE,"E135"),sQuery(id+"F0.wireOp",EDGE,"E136"),sQuery(id+"F0.wireOp",EDGE,"E137"),sQuery(id+"F0.wireOp",EDGE,"E138"),sQuery(id+"F0.wireOp",EDGE,"E139"),sQuery(id+"F0.wireOp",EDGE,"E140"),sQuery(id+"F0.wireOp",EDGE,"E141"),sQuery(id+"F0.wireOp",EDGE,"E142"),sQuery(id+"F0.wireOp",EDGE,"E143"),sQuery(id+"F0.wireOp",EDGE,"E144"),sQuery(id+"F0.wireOp",EDGE,"E145"),sQuery(id+"F0.wireOp",EDGE,"E146"),sQuery(id+"F0.wireOp",EDGE,"E147"),sQuery(id+"F0.wireOp",EDGE,"E148"),sQuery(id+"F0.wireOp",EDGE,"E149"),sQuery(id+"F0.wireOp",EDGE,"E150"),sQuery(id+"F0.wireOp",EDGE,"E151"),sQuery(id+"F0.wireOp",EDGE,"E152"),sQuery(id+"F0.wireOp",EDGE,"E153"),sQuery(id+"F0.wireOp",EDGE,"E154"),sQuery(id+"F0.wireOp",EDGE,"E155"),sQuery(id+"F0.wireOp",EDGE,"E156"),sQuery(id+"F0.wireOp",EDGE,"E157"),sQuery(id+"F0.wireOp",EDGE,"E158"),sQuery(id+"F0.wireOp",EDGE,"E159"),sQuery(id+"F0.wireOp",EDGE,"E160"),sQuery(id+"F0.wireOp",EDGE,"E161"),sQuery(id+"F0.wireOp",EDGE,"E162"),sQuery(id+"F0.wireOp",EDGE,"E163"),sQuery(id+"F0.wireOp",EDGE,"E164"),sQuery(id+"F0.wireOp",EDGE,"E165"),sQuery(id+"F0.wireOp",EDGE,"E166"),sQuery(id+"F0.wireOp",EDGE,"E167"),sQuery(id+"F0.wireOp",EDGE,"E168"),sQuery(id+"F0.wireOp",EDGE,"E169"),sQuery(id+"F0.wireOp",EDGE,"E170"),sQuery(id+"F0.wireOp",EDGE,"E171"),sQuery(id+"F0.wireOp",EDGE,"E172"),sQuery(id+"F0.wireOp",EDGE,"E173"),sQuery(id+"F0.wireOp",EDGE,"E174"),sQuery(id+"F0.wireOp",EDGE,"E175"),sQuery(id+"F0.wireOp",EDGE,"E176"),sQuery(id+"F0.wireOp",EDGE,"E177"),sQuery(id+"F0.wireOp",EDGE,"E178"),sQuery(id+"F0.wireOp",EDGE,"E179"),sQuery(id+"F0.wireOp",EDGE,"E180"),sQuery(id+"F0.wireOp",EDGE,"E181"),sQuery(id+"F0.wireOp",EDGE,"E182"),sQuery(id+"F0.wireOp",EDGE,"E183"),sQuery(id+"F0.wireOp",EDGE,"E184"),sQuery(id+"F0.wireOp",EDGE,"E185"),sQuery(id+"F0.wireOp",EDGE,"E186"),sQuery(id+"F0.wireOp",EDGE,"E187"),sQuery(id+"F0.wireOp",EDGE,"E188"),sQuery(id+"F0.wireOp",EDGE,"E189"),sQuery(id+"F0.wireOp",EDGE,"E190"),sQuery(id+"F0.wireOp",EDGE,"E191"),sQuery(id+"F0.wireOp",EDGE,"E192"),sQuery(id+"F0.wireOp",EDGE,"E193"),sQuery(id+"F0.wireOp",EDGE,"E194"),sQuery(id+"F0.wireOp",EDGE,"E195"),sQuery(id+"F0.wireOp",EDGE,"E196"),sQuery(id+"F0.wireOp",EDGE,"E197"),sQuery(id+"F0.wireOp",EDGE,"E198"),sQuery(id+"F0.wireOp",EDGE,"E199"),sQuery(id+"F0.wireOp",EDGE,"E200"),sQuery(id+"F0.wireOp",EDGE,"E201"),sQuery(id+"F0.wireOp",EDGE,"E202"),sQuery(id+"F0.wireOp",EDGE,"E203"),sQuery(id+"F0.wireOp",EDGE,"E204"),sQuery(id+"F0.wireOp",EDGE,"E205"),sQuery(id+"F0.wireOp",EDGE,"E206"),sQuery(id+"F0.wireOp",EDGE,"E207"),sQuery(id+"F0.wireOp",EDGE,"E208"),sQuery(id+"F0.wireOp",EDGE,"E209"),sQuery(id+"F0.wireOp",EDGE,"E210"),sQuery(id+"F0.wireOp",EDGE,"E211"),sQuery(id+"F0.wireOp",EDGE,"E212"),sQuery(id+"F0.wireOp",EDGE,"E213"),sQuery(id+"F0.wireOp",EDGE,"E214"),sQuery(id+"F0.wireOp",EDGE,"E215"),sQuery(id+"F0.wireOp",EDGE,"E216"),sQuery(id+"F0.wireOp",EDGE,"E217"),sQuery(id+"F0.wireOp",EDGE,"E218"),sQuery(id+"F0.wireOp",EDGE,"E219"),sQuery(id+"F0.wireOp",EDGE,"E220"),sQuery(id+"F0.wireOp",EDGE,"E221"),sQuery(id+"F0.wireOp",EDGE,"E222"),sQuery(id+"F0.wireOp",EDGE,"E223"),sQuery(id+"F0.wireOp",EDGE,"E224"),sQuery(id+"F0.wireOp",EDGE,"E225"),sQuery(id+"F0.wireOp",EDGE,"E226"),sQuery(id+"F0.wireOp",EDGE,"E227"),sQuery(id+"F0.wireOp",EDGE,"E228"),sQuery(id+"F0.wireOp",EDGE,"E229"),sQuery(id+"F0.wireOp",EDGE,"E230"),sQuery(id+"F0.wireOp",EDGE,"E231"),sQuery(id+"F0.wireOp",EDGE,"E232"),sQuery(id+"F0.wireOp",EDGE,"E233"),sQuery(id+"F0.wireOp",EDGE,"E234"),sQuery(id+"F0.wireOp",EDGE,"E235"),sQuery(id+"F0.wireOp",EDGE,"E236"),sQuery(id+"F0.wireOp",EDGE,"E237"),sQuery(id+"F0.wireOp",EDGE,"E238"),sQuery(id+"F0.wireOp",EDGE,"E239"),sQuery(id+"F0.wireOp",EDGE,"E240"),sQuery(id+"F0.wireOp",EDGE,"E241"),sQuery(id+"F0.wireOp",EDGE,"E242"),sQuery(id+"F0.wireOp",EDGE,"E243"),sQuery(id+"F0.wireOp",EDGE,"E244"),sQuery(id+"F0.wireOp",EDGE,"E245"),sQuery(id+"F0.wireOp",EDGE,"E246"),sQuery(id+"F0.wireOp",EDGE,"E247"),sQuery(id+"F0.wireOp",EDGE,"E248"),sQuery(id+"F0.wireOp",EDGE,"E249"),sQuery(id+"F0.wireOp",EDGE,"E250"),sQuery(id+"F0.wireOp",EDGE,"E251"),sQuery(id+"F0.wireOp",EDGE,"E252"),sQuery(id+"F0.wireOp",EDGE,"E253"),sQuery(id+"F0.wireOp",EDGE,"E254"),sQuery(id+"F0.wireOp",EDGE,"E255"),sQuery(id+"F0.wireOp",EDGE,"E256"),sQuery(id+"F0.wireOp",EDGE,"E257"),sQuery(id+"F0.wireOp",EDGE,"E258"),sQuery(id+"F0.wireOp",EDGE,"E259"),sQuery(id+"F0.wireOp",EDGE,"E260"),sQuery(id+"F0.wireOp",EDGE,"E261"),sQuery(id+"F0.wireOp",EDGE,"E262"),sQuery(id+"F0.wireOp",EDGE,"E263"),sQuery(id+"F0.wireOp",EDGE,"E264"),sQuery(id+"F0.wireOp",EDGE,"E265"),sQuery(id+"F0.wireOp",EDGE,"E266"),sQuery(id+"F0.wireOp",EDGE,"E267"),sQuery(id+"F0.wireOp",EDGE,"E268"),sQuery(id+"F0.wireOp",EDGE,"E269"),sQuery(id+"F0.wireOp",EDGE,"E270"),sQuery(id+"F0.wireOp",EDGE,"E271"),sQuery(id+"F0.wireOp",EDGE,"E272"),sQuery(id+"F0.wireOp",EDGE,"E273"),sQuery(id+"F0.wireOp",EDGE,"E274"),sQuery(id+"F0.wireOp",EDGE,"E275"),sQuery(id+"F0.wireOp",EDGE,"E276"),sQuery(id+"F0.wireOp",EDGE,"E277"),sQuery(id+"F0.wireOp",EDGE,"E278"),sQuery(id+"F0.wireOp",EDGE,"E279"),sQuery(id+"F0.wireOp",EDGE,"E280"),sQuery(id+"F0.wireOp",EDGE,"E281"),sQuery(id+"F0.wireOp",EDGE,"E282"),sQuery(id+"F0.wireOp",EDGE,"E283"),sQuery(id+"F0.wireOp",EDGE,"E284"),sQuery(id+"F0.wireOp",EDGE,"E285"),sQuery(id+"F0.wireOp",EDGE,"E286"),sQuery(id+"F0.wireOp",EDGE,"E287"),sQuery(id+"F0.wireOp",EDGE,"E288"),sQuery(id+"F0.wireOp",EDGE,"E289"),sQuery(id+"F0.wireOp",EDGE,"E290"),sQuery(id+"F0.wireOp",EDGE,"E291"),sQuery(id+"F0.wireOp",EDGE,"E292"),sQuery(id+"F0.wireOp",EDGE,"E293"),sQuery(id+"F0.wireOp",EDGE,"E294"),sQuery(id+"F0.wireOp",EDGE,"E295"),sQuery(id+"F0.wireOp",EDGE,"E296"),sQuery(id+"F0.wireOp",EDGE,"E297"),sQuery(id+"F0.wireOp",EDGE,"E298"),sQuery(id+"F0.wireOp",EDGE,"E299"),sQuery(id+"F0.wireOp",EDGE,"E300"),sQuery(id+"F0.wireOp",EDGE,"E301"),sQuery(id+"F0.wireOp",EDGE,"E302"),sQuery(id+"F0.wireOp",EDGE,"E303"),sQuery(id+"F0.wireOp",EDGE,"E304"),sQuery(id+"F0.wireOp",EDGE,"E305"),sQuery(id+"F0.wireOp",EDGE,"E306"),sQuery(id+"F0.wireOp",EDGE,"E307"),sQuery(id+"F0.wireOp",EDGE,"E308"),sQuery(id+"F0.wireOp",EDGE,"E309"),sQuery(id+"F0.wireOp",EDGE,"E310"),sQuery(id+"F0.wireOp",EDGE,"E311"),sQuery(id+"F0.wireOp",EDGE,"E312"),sQuery(id+"F0.wireOp",EDGE,"E313"),sQuery(id+"F0.wireOp",EDGE,"E314"),sQuery(id+"F0.wireOp",EDGE,"E315"),sQuery(id+"F0.wireOp",EDGE,"E316"),sQuery(id+"F0.wireOp",EDGE,"E317"),sQuery(id+"F0.wireOp",EDGE,"E318"),sQuery(id+"F0.wireOp",EDGE,"E319"),sQuery(id+"F0.wireOp",EDGE,"E320"),sQuery(id+"F0.wireOp",EDGE,"E321")])],"isStart":false});
            var sketch = newSketch(context, id + "F2", { "sketchPlane" : qUnion([Q0])});
            skCircle(sketch, "E322", {"center": v(-3.78, 6.65) * mm, "radius": 2.75 * mm});
            skSolve(sketch);
        }
        {
            var Q0;
            Q0 = qSketchRegion(id + "F2", true);
            extrude(context, id + "F3", {"entities" : qUnion([Q0]), "operationType" : NewBodyOperationType.REMOVE, "oppositeDirection" : true, "depth" : 25 * mm});
        }
        {
            var Q0;
            Q0=makeQuery(id+"F1.opExtrude","CAP_FACE",FACE,{"disambiguationData":[OSD([sQuery(id+"F0.wireOp",EDGE,"E1"),sQuery(id+"F0.wireOp",EDGE,"E2"),sQuery(id+"F0.wireOp",EDGE,"E3"),sQuery(id+"F0.wireOp",EDGE,"E4"),sQuery(id+"F0.wireOp",EDGE,"E5"),sQuery(id+"F0.wireOp",EDGE,"E6"),sQuery(id+"F0.wireOp",EDGE,"E7"),sQuery(id+"F0.wireOp",EDGE,"E8"),sQuery(id+"F0.wireOp",EDGE,"E9"),sQuery(id+"F0.wireOp",EDGE,"E10"),sQuery(id+"F0.wireOp",EDGE,"E11"),sQuery(id+"F0.wireOp",EDGE,"E12"),sQuery(id+"F0.wireOp",EDGE,"E13"),sQuery(id+"F0.wireOp",EDGE,"E14"),sQuery(id+"F0.wireOp",EDGE,"E15"),sQuery(id+"F0.wireOp",EDGE,"E16"),sQuery(id+"F0.wireOp",EDGE,"E17"),sQuery(id+"F0.wireOp",EDGE,"E18"),sQuery(id+"F0.wireOp",EDGE,"E19"),sQuery(id+"F0.wireOp",EDGE,"E20"),sQuery(id+"F0.wireOp",EDGE,"E21"),sQuery(id+"F0.wireOp",EDGE,"E22"),sQuery(id+"F0.wireOp",EDGE,"E23"),sQuery(id+"F0.wireOp",EDGE,"E24"),sQuery(id+"F0.wireOp",EDGE,"E25"),sQuery(id+"F0.wireOp",EDGE,"E26"),sQuery(id+"F0.wireOp",EDGE,"E27"),sQuery(id+"F0.wireOp",EDGE,"E28"),sQuery(id+"F0.wireOp",EDGE,"E29"),sQuery(id+"F0.wireOp",EDGE,"E30"),sQuery(id+"F0.wireOp",EDGE,"E31"),sQuery(id+"F0.wireOp",EDGE,"E32"),sQuery(id+"F0.wireOp",EDGE,"E33"),sQuery(id+"F0.wireOp",EDGE,"E34"),sQuery(id+"F0.wireOp",EDGE,"E35"),sQuery(id+"F0.wireOp",EDGE,"E36"),sQuery(id+"F0.wireOp",EDGE,"E37"),sQuery(id+"F0.wireOp",EDGE,"E38"),sQuery(id+"F0.wireOp",EDGE,"E39"),sQuery(id+"F0.wireOp",EDGE,"E40"),sQuery(id+"F0.wireOp",EDGE,"E41"),sQuery(id+"F0.wireOp",EDGE,"E42"),sQuery(id+"F0.wireOp",EDGE,"E43"),sQuery(id+"F0.wireOp",EDGE,"E44"),sQuery(id+"F0.wireOp",EDGE,"E45"),sQuery(id+"F0.wireOp",EDGE,"E46"),sQuery(id+"F0.wireOp",EDGE,"E47"),sQuery(id+"F0.wireOp",EDGE,"E48"),sQuery(id+"F0.wireOp",EDGE,"E49"),sQuery(id+"F0.wireOp",EDGE,"E50"),sQuery(id+"F0.wireOp",EDGE,"E51"),sQuery(id+"F0.wireOp",EDGE,"E52"),sQuery(id+"F0.wireOp",EDGE,"E53"),sQuery(id+"F0.wireOp",EDGE,"E54"),sQuery(id+"F0.wireOp",EDGE,"E55"),sQuery(id+"F0.wireOp",EDGE,"E56"),sQuery(id+"F0.wireOp",EDGE,"E57"),sQuery(id+"F0.wireOp",EDGE,"E58"),sQuery(id+"F0.wireOp",EDGE,"E59"),sQuery(id+"F0.wireOp",EDGE,"E60"),sQuery(id+"F0.wireOp",EDGE,"E61"),sQuery(id+"F0.wireOp",EDGE,"E62"),sQuery(id+"F0.wireOp",EDGE,"E63"),sQuery(id+"F0.wireOp",EDGE,"E64"),sQuery(id+"F0.wireOp",EDGE,"E65"),sQuery(id+"F0.wireOp",EDGE,"E66"),sQuery(id+"F0.wireOp",EDGE,"E67"),sQuery(id+"F0.wireOp",EDGE,"E68"),sQuery(id+"F0.wireOp",EDGE,"E69"),sQuery(id+"F0.wireOp",EDGE,"E70"),sQuery(id+"F0.wireOp",EDGE,"E71"),sQuery(id+"F0.wireOp",EDGE,"E72"),sQuery(id+"F0.wireOp",EDGE,"E73"),sQuery(id+"F0.wireOp",EDGE,"E74"),sQuery(id+"F0.wireOp",EDGE,"E75"),sQuery(id+"F0.wireOp",EDGE,"E76"),sQuery(id+"F0.wireOp",EDGE,"E77"),sQuery(id+"F0.wireOp",EDGE,"E78"),sQuery(id+"F0.wireOp",EDGE,"E79"),sQuery(id+"F0.wireOp",EDGE,"E80"),sQuery(id+"F0.wireOp",EDGE,"E81"),sQuery(id+"F0.wireOp",EDGE,"E82"),sQuery(id+"F0.wireOp",EDGE,"E83"),sQuery(id+"F0.wireOp",EDGE,"E84"),sQuery(id+"F0.wireOp",EDGE,"E85"),sQuery(id+"F0.wireOp",EDGE,"E86"),sQuery(id+"F0.wireOp",EDGE,"E87"),sQuery(id+"F0.wireOp",EDGE,"E88"),sQuery(id+"F0.wireOp",EDGE,"E89"),sQuery(id+"F0.wireOp",EDGE,"E90"),sQuery(id+"F0.wireOp",EDGE,"E91"),sQuery(id+"F0.wireOp",EDGE,"E92"),sQuery(id+"F0.wireOp",EDGE,"E93"),sQuery(id+"F0.wireOp",EDGE,"E94"),sQuery(id+"F0.wireOp",EDGE,"E95"),sQuery(id+"F0.wireOp",EDGE,"E96"),sQuery(id+"F0.wireOp",EDGE,"E97"),sQuery(id+"F0.wireOp",EDGE,"E98"),sQuery(id+"F0.wireOp",EDGE,"E99"),sQuery(id+"F0.wireOp",EDGE,"E100"),sQuery(id+"F0.wireOp",EDGE,"E101"),sQuery(id+"F0.wireOp",EDGE,"E102"),sQuery(id+"F0.wireOp",EDGE,"E103"),sQuery(id+"F0.wireOp",EDGE,"E104"),sQuery(id+"F0.wireOp",EDGE,"E105"),sQuery(id+"F0.wireOp",EDGE,"E106"),sQuery(id+"F0.wireOp",EDGE,"E107"),sQuery(id+"F0.wireOp",EDGE,"E108"),sQuery(id+"F0.wireOp",EDGE,"E109"),sQuery(id+"F0.wireOp",EDGE,"E110"),sQuery(id+"F0.wireOp",EDGE,"E111"),sQuery(id+"F0.wireOp",EDGE,"E112"),sQuery(id+"F0.wireOp",EDGE,"E113"),sQuery(id+"F0.wireOp",EDGE,"E114"),sQuery(id+"F0.wireOp",EDGE,"E115"),sQuery(id+"F0.wireOp",EDGE,"E116"),sQuery(id+"F0.wireOp",EDGE,"E117"),sQuery(id+"F0.wireOp",EDGE,"E118"),sQuery(id+"F0.wireOp",EDGE,"E119"),sQuery(id+"F0.wireOp",EDGE,"E120"),sQuery(id+"F0.wireOp",EDGE,"E121"),sQuery(id+"F0.wireOp",EDGE,"E122"),sQuery(id+"F0.wireOp",EDGE,"E123"),sQuery(id+"F0.wireOp",EDGE,"E124"),sQuery(id+"F0.wireOp",EDGE,"E125"),sQuery(id+"F0.wireOp",EDGE,"E126"),sQuery(id+"F0.wireOp",EDGE,"E127"),sQuery(id+"F0.wireOp",EDGE,"E128"),sQuery(id+"F0.wireOp",EDGE,"E129"),sQuery(id+"F0.wireOp",EDGE,"E130"),sQuery(id+"F0.wireOp",EDGE,"E131"),sQuery(id+"F0.wireOp",EDGE,"E132"),sQuery(id+"F0.wireOp",EDGE,"E133"),sQuery(id+"F0.wireOp",EDGE,"E134"),sQuery(id+"F0.wireOp",EDGE,"E135"),sQuery(id+"F0.wireOp",EDGE,"E136"),sQuery(id+"F0.wireOp",EDGE,"E137"),sQuery(id+"F0.wireOp",EDGE,"E138"),sQuery(id+"F0.wireOp",EDGE,"E139"),sQuery(id+"F0.wireOp",EDGE,"E140"),sQuery(id+"F0.wireOp",EDGE,"E141"),sQuery(id+"F0.wireOp",EDGE,"E142"),sQuery(id+"F0.wireOp",EDGE,"E143"),sQuery(id+"F0.wireOp",EDGE,"E144"),sQuery(id+"F0.wireOp",EDGE,"E145"),sQuery(id+"F0.wireOp",EDGE,"E146"),sQuery(id+"F0.wireOp",EDGE,"E147"),sQuery(id+"F0.wireOp",EDGE,"E148"),sQuery(id+"F0.wireOp",EDGE,"E149"),sQuery(id+"F0.wireOp",EDGE,"E150"),sQuery(id+"F0.wireOp",EDGE,"E151"),sQuery(id+"F0.wireOp",EDGE,"E152"),sQuery(id+"F0.wireOp",EDGE,"E153"),sQuery(id+"F0.wireOp",EDGE,"E154"),sQuery(id+"F0.wireOp",EDGE,"E155"),sQuery(id+"F0.wireOp",EDGE,"E156"),sQuery(id+"F0.wireOp",EDGE,"E157"),sQuery(id+"F0.wireOp",EDGE,"E158"),sQuery(id+"F0.wireOp",EDGE,"E159"),sQuery(id+"F0.wireOp",EDGE,"E160"),sQuery(id+"F0.wireOp",EDGE,"E161"),sQuery(id+"F0.wireOp",EDGE,"E162"),sQuery(id+"F0.wireOp",EDGE,"E163"),sQuery(id+"F0.wireOp",EDGE,"E164"),sQuery(id+"F0.wireOp",EDGE,"E165"),sQuery(id+"F0.wireOp",EDGE,"E166"),sQuery(id+"F0.wireOp",EDGE,"E167"),sQuery(id+"F0.wireOp",EDGE,"E168"),sQuery(id+"F0.wireOp",EDGE,"E169"),sQuery(id+"F0.wireOp",EDGE,"E170"),sQuery(id+"F0.wireOp",EDGE,"E171"),sQuery(id+"F0.wireOp",EDGE,"E172"),sQuery(id+"F0.wireOp",EDGE,"E173"),sQuery(id+"F0.wireOp",EDGE,"E174"),sQuery(id+"F0.wireOp",EDGE,"E175"),sQuery(id+"F0.wireOp",EDGE,"E176"),sQuery(id+"F0.wireOp",EDGE,"E177"),sQuery(id+"F0.wireOp",EDGE,"E178"),sQuery(id+"F0.wireOp",EDGE,"E179"),sQuery(id+"F0.wireOp",EDGE,"E180"),sQuery(id+"F0.wireOp",EDGE,"E181"),sQuery(id+"F0.wireOp",EDGE,"E182"),sQuery(id+"F0.wireOp",EDGE,"E183"),sQuery(id+"F0.wireOp",EDGE,"E184"),sQuery(id+"F0.wireOp",EDGE,"E185"),sQuery(id+"F0.wireOp",EDGE,"E186"),sQuery(id+"F0.wireOp",EDGE,"E187"),sQuery(id+"F0.wireOp",EDGE,"E188"),sQuery(id+"F0.wireOp",EDGE,"E189"),sQuery(id+"F0.wireOp",EDGE,"E190"),sQuery(id+"F0.wireOp",EDGE,"E191"),sQuery(id+"F0.wireOp",EDGE,"E192"),sQuery(id+"F0.wireOp",EDGE,"E193"),sQuery(id+"F0.wireOp",EDGE,"E194"),sQuery(id+"F0.wireOp",EDGE,"E195"),sQuery(id+"F0.wireOp",EDGE,"E196"),sQuery(id+"F0.wireOp",EDGE,"E197"),sQuery(id+"F0.wireOp",EDGE,"E198"),sQuery(id+"F0.wireOp",EDGE,"E199"),sQuery(id+"F0.wireOp",EDGE,"E200"),sQuery(id+"F0.wireOp",EDGE,"E201"),sQuery(id+"F0.wireOp",EDGE,"E202"),sQuery(id+"F0.wireOp",EDGE,"E203"),sQuery(id+"F0.wireOp",EDGE,"E204"),sQuery(id+"F0.wireOp",EDGE,"E205"),sQuery(id+"F0.wireOp",EDGE,"E206"),sQuery(id+"F0.wireOp",EDGE,"E207"),sQuery(id+"F0.wireOp",EDGE,"E208"),sQuery(id+"F0.wireOp",EDGE,"E209"),sQuery(id+"F0.wireOp",EDGE,"E210"),sQuery(id+"F0.wireOp",EDGE,"E211"),sQuery(id+"F0.wireOp",EDGE,"E212"),sQuery(id+"F0.wireOp",EDGE,"E213"),sQuery(id+"F0.wireOp",EDGE,"E214"),sQuery(id+"F0.wireOp",EDGE,"E215"),sQuery(id+"F0.wireOp",EDGE,"E216"),sQuery(id+"F0.wireOp",EDGE,"E217"),sQuery(id+"F0.wireOp",EDGE,"E218"),sQuery(id+"F0.wireOp",EDGE,"E219"),sQuery(id+"F0.wireOp",EDGE,"E220"),sQuery(id+"F0.wireOp",EDGE,"E221"),sQuery(id+"F0.wireOp",EDGE,"E222"),sQuery(id+"F0.wireOp",EDGE,"E223"),sQuery(id+"F0.wireOp",EDGE,"E224"),sQuery(id+"F0.wireOp",EDGE,"E225"),sQuery(id+"F0.wireOp",EDGE,"E226"),sQuery(id+"F0.wireOp",EDGE,"E227"),sQuery(id+"F0.wireOp",EDGE,"E228"),sQuery(id+"F0.wireOp",EDGE,"E229"),sQuery(id+"F0.wireOp",EDGE,"E230"),sQuery(id+"F0.wireOp",EDGE,"E231"),sQuery(id+"F0.wireOp",EDGE,"E232"),sQuery(id+"F0.wireOp",EDGE,"E233"),sQuery(id+"F0.wireOp",EDGE,"E234"),sQuery(id+"F0.wireOp",EDGE,"E235"),sQuery(id+"F0.wireOp",EDGE,"E236"),sQuery(id+"F0.wireOp",EDGE,"E237"),sQuery(id+"F0.wireOp",EDGE,"E238"),sQuery(id+"F0.wireOp",EDGE,"E239"),sQuery(id+"F0.wireOp",EDGE,"E240"),sQuery(id+"F0.wireOp",EDGE,"E241"),sQuery(id+"F0.wireOp",EDGE,"E242"),sQuery(id+"F0.wireOp",EDGE,"E243"),sQuery(id+"F0.wireOp",EDGE,"E244"),sQuery(id+"F0.wireOp",EDGE,"E245"),sQuery(id+"F0.wireOp",EDGE,"E246"),sQuery(id+"F0.wireOp",EDGE,"E247"),sQuery(id+"F0.wireOp",EDGE,"E248"),sQuery(id+"F0.wireOp",EDGE,"E249"),sQuery(id+"F0.wireOp",EDGE,"E250"),sQuery(id+"F0.wireOp",EDGE,"E251"),sQuery(id+"F0.wireOp",EDGE,"E252"),sQuery(id+"F0.wireOp",EDGE,"E253"),sQuery(id+"F0.wireOp",EDGE,"E254"),sQuery(id+"F0.wireOp",EDGE,"E255"),sQuery(id+"F0.wireOp",EDGE,"E256"),sQuery(id+"F0.wireOp",EDGE,"E257"),sQuery(id+"F0.wireOp",EDGE,"E258"),sQuery(id+"F0.wireOp",EDGE,"E259"),sQuery(id+"F0.wireOp",EDGE,"E260"),sQuery(id+"F0.wireOp",EDGE,"E261"),sQuery(id+"F0.wireOp",EDGE,"E262"),sQuery(id+"F0.wireOp",EDGE,"E263"),sQuery(id+"F0.wireOp",EDGE,"E264"),sQuery(id+"F0.wireOp",EDGE,"E265"),sQuery(id+"F0.wireOp",EDGE,"E266"),sQuery(id+"F0.wireOp",EDGE,"E267"),sQuery(id+"F0.wireOp",EDGE,"E268"),sQuery(id+"F0.wireOp",EDGE,"E269"),sQuery(id+"F0.wireOp",EDGE,"E270"),sQuery(id+"F0.wireOp",EDGE,"E271"),sQuery(id+"F0.wireOp",EDGE,"E272"),sQuery(id+"F0.wireOp",EDGE,"E273"),sQuery(id+"F0.wireOp",EDGE,"E274"),sQuery(id+"F0.wireOp",EDGE,"E275"),sQuery(id+"F0.wireOp",EDGE,"E276"),sQuery(id+"F0.wireOp",EDGE,"E277"),sQuery(id+"F0.wireOp",EDGE,"E278"),sQuery(id+"F0.wireOp",EDGE,"E279"),sQuery(id+"F0.wireOp",EDGE,"E280"),sQuery(id+"F0.wireOp",EDGE,"E281"),sQuery(id+"F0.wireOp",EDGE,"E282"),sQuery(id+"F0.wireOp",EDGE,"E283"),sQuery(id+"F0.wireOp",EDGE,"E284"),sQuery(id+"F0.wireOp",EDGE,"E285"),sQuery(id+"F0.wireOp",EDGE,"E286"),sQuery(id+"F0.wireOp",EDGE,"E287"),sQuery(id+"F0.wireOp",EDGE,"E288"),sQuery(id+"F0.wireOp",EDGE,"E289"),sQuery(id+"F0.wireOp",EDGE,"E290"),sQuery(id+"F0.wireOp",EDGE,"E291"),sQuery(id+"F0.wireOp",EDGE,"E292"),sQuery(id+"F0.wireOp",EDGE,"E293"),sQuery(id+"F0.wireOp",EDGE,"E294"),sQuery(id+"F0.wireOp",EDGE,"E295"),sQuery(id+"F0.wireOp",EDGE,"E296"),sQuery(id+"F0.wireOp",EDGE,"E297"),sQuery(id+"F0.wireOp",EDGE,"E298"),sQuery(id+"F0.wireOp",EDGE,"E299"),sQuery(id+"F0.wireOp",EDGE,"E300"),sQuery(id+"F0.wireOp",EDGE,"E301"),sQuery(id+"F0.wireOp",EDGE,"E302"),sQuery(id+"F0.wireOp",EDGE,"E303"),sQuery(id+"F0.wireOp",EDGE,"E304"),sQuery(id+"F0.wireOp",EDGE,"E305"),sQuery(id+"F0.wireOp",EDGE,"E306"),sQuery(id+"F0.wireOp",EDGE,"E307"),sQuery(id+"F0.wireOp",EDGE,"E308"),sQuery(id+"F0.wireOp",EDGE,"E309"),sQuery(id+"F0.wireOp",EDGE,"E310"),sQuery(id+"F0.wireOp",EDGE,"E311"),sQuery(id+"F0.wireOp",EDGE,"E312"),sQuery(id+"F0.wireOp",EDGE,"E313"),sQuery(id+"F0.wireOp",EDGE,"E314"),sQuery(id+"F0.wireOp",EDGE,"E315"),sQuery(id+"F0.wireOp",EDGE,"E316"),sQuery(id+"F0.wireOp",EDGE,"E317"),sQuery(id+"F0.wireOp",EDGE,"E318"),sQuery(id+"F0.wireOp",EDGE,"E319"),sQuery(id+"F0.wireOp",EDGE,"E320"),sQuery(id+"F0.wireOp",EDGE,"E321")])],"isStart":false});
            var sketch = newSketch(context, id + "F4", { "sketchPlane" : qUnion([Q0])});
            skText(sketch, "E323", { "text": "FREYA\n", "fontName": "OpenSans-Regular.ttf"});
            const initialGuessF4  = {"E323": [-0.02294, 0.05004, 0, -1, 0.00506]};
            skSetInitialGuess(sketch, initialGuessF4);
            skSolve(sketch);
        }
        {
            var Q0;
            Q0 = qSketchRegion(id + "F4", true);
            extrude(context, id + "F5", {"entities" : qUnion([Q0]), "operationType" : NewBodyOperationType.ADD, "depth" : 1 * mm});
        }
    });
